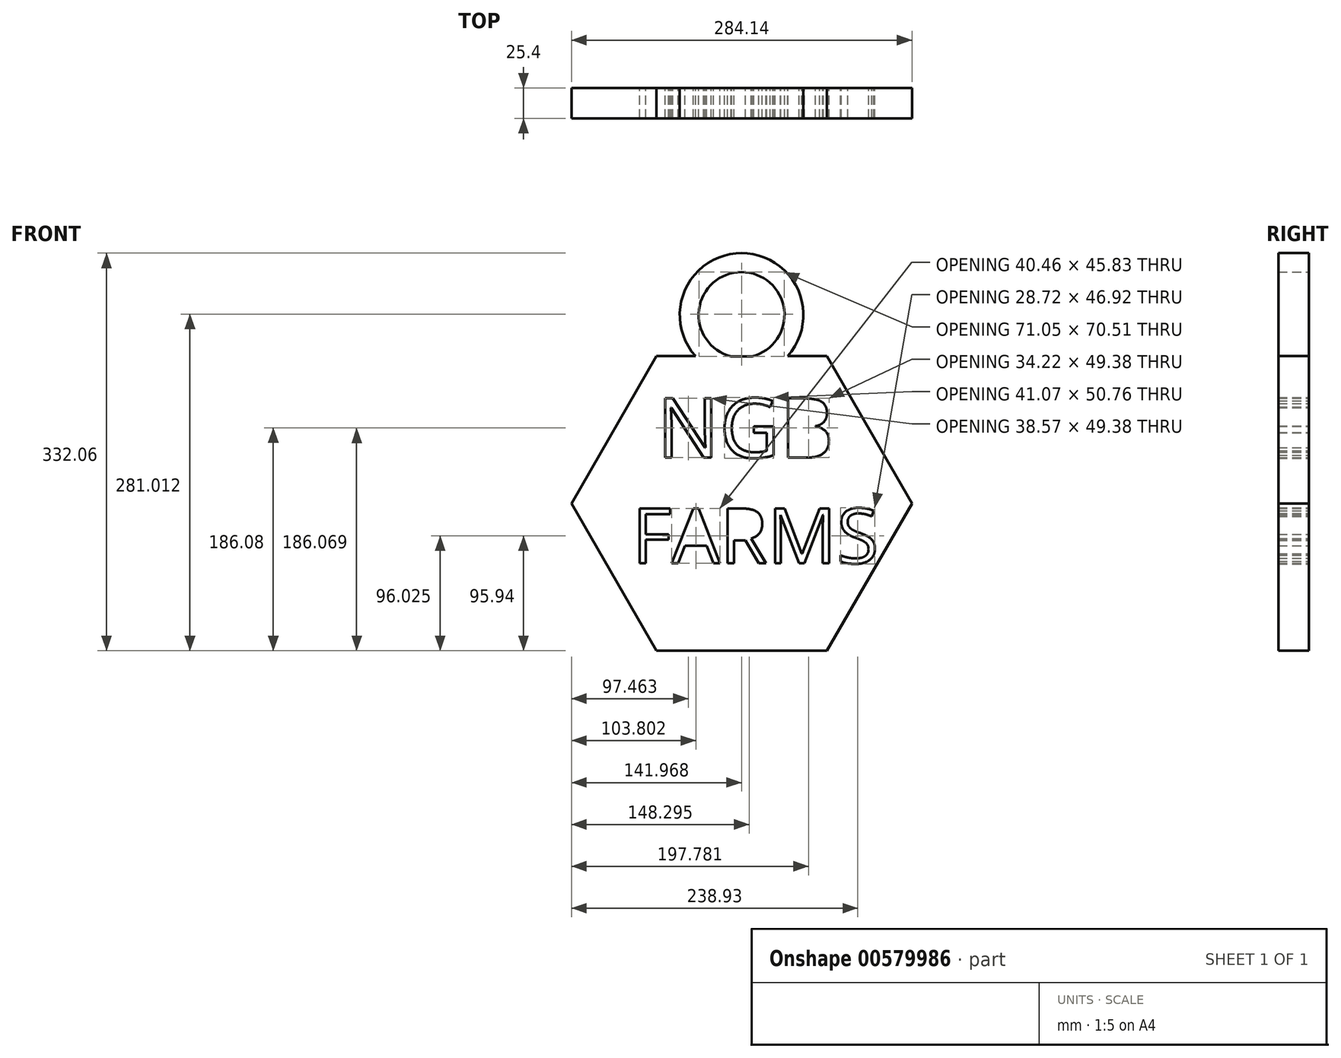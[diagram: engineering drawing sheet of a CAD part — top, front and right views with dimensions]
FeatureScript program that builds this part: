
annotation { "Feature Type Name" : "Feature", "Feature Type Description" : "" }
export const myFeature = defineFeature(function(context is Context, id is Id, definition is map)
    precondition{}
    {
        {
            var Q0;
            Q0=qCreatedBy(makeId("Front.planeOp"),FACE);
            var sketch = newSketch(context, id + "F0", { "sketchPlane" : qUnion([Q0])});
            skArc(sketch, "E0.cCircle", {"start": v(-108.28, 192.27) * mm, "mid": v(-99.34, -53.49) * mm, "end": v(-90.7, 192.28) * mm, "construction": true});
            skLineSegment(sketch, "E0.0", {"start": v(42.65, 69.54) * mm, "end": v(-28.39, -53.5) * mm});
            skLineSegment(sketch, "E0.1", {"start": v(-28.39, -53.5) * mm, "end": v(-170.46, -53.49) * mm});
            skLineSegment(sketch, "E0.2", {"start": v(-170.46, -53.49) * mm, "end": v(-241.5, 69.55) * mm});
            skLineSegment(sketch, "E0.3", {"start": v(-241.5, 69.55) * mm, "end": v(-170.45, 192.59) * mm});
            skLineSegment(sketch, "E0.4", {"start": v(-170.45, 192.59) * mm, "end": v(-137.98, 192.59) * mm});
            skLineSegment(sketch, "E0.5", {"start": v(-28.38, 192.58) * mm, "end": v(42.65, 69.54) * mm});
            skPoint(sketch, "E0.0.midPoint", {"position": v(7.13, 8.02) * mm});
            skArc(sketch, "E1", {"start": v(-61.06, 192.58) * mm, "mid": v(-99.52, 278.57) * mm, "end": v(-137.98, 192.59) * mm});
            skArc(sketch, "E2", {"start": v(-90.7, 192.28) * mm, "mid": v(-99.54, 262.78) * mm, "end": v(-108.28, 192.27) * mm});
            skLineSegment(sketch, "E3.trimOffspring", {"start": v(-61.06, 192.58) * mm, "end": v(-28.38, 192.58) * mm});
            skText(sketch, "E4", { "text": "NGB", "fontName": "OpenSans-Regular.ttf"});
            skText(sketch, "E5", { "text": "FARMS", "fontName": "OpenSans-Regular.ttf"});
            skLineSegment(sketch, "E6.0", {"start": v(-236, 66.38) * mm, "end": v(-164.95, 189.41) * mm});
            skLineSegment(sketch, "E7.0", {"start": v(-164.96, -50.31) * mm, "end": v(-236, 72.73) * mm});
            skLineSegment(sketch, "E8.0", {"start": v(-28.39, -59.84) * mm, "end": v(-170.46, -59.84) * mm});
            skLineSegment(sketch, "E9.0", {"start": v(-22.88, 195.76) * mm, "end": v(48.15, 72.72) * mm});
            skLineSegment(sketch, "E10.0", {"start": v(48.15, 66.37) * mm, "end": v(-22.89, -56.67) * mm});
            skLineSegment(sketch, "E11.0", {"start": v(-61.06, 198.93) * mm, "end": v(-28.38, 198.93) * mm});
            skLineSegment(sketch, "E12.0", {"start": v(-170.45, 198.94) * mm, "end": v(-137.98, 198.94) * mm});
            skLineSegment(sketch, "E13", {"start": v(-108.28, 192.27) * mm, "end": v(-90.7, 192.28) * mm});
            const initialGuessF0  = {"E4": [-0.1701, 0.10789, 1, 0, 0.0498], "E5": [-0.19091, 0.01962, 1, 0, 0.04603]};
            skSetInitialGuess(sketch, initialGuessF0);
            skSolve(sketch);
        }
        {
            var Q0;
            Q0 = qSketchRegion(id + "F0", true);
            extrude(context, id + "F1", {"entities" : qUnion([Q0]), "depth" : 25.4 * mm, "offsetDistance" : 25.4 * mm});
        }
    });
